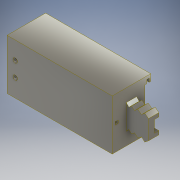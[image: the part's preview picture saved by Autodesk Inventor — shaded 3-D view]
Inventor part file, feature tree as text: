
AUTODESK INVENTOR PART (.ipt)
format: ipt  version: 2018 (Build 220112000, 112)  size: 280,576 bytes
history: native  units: mm
features: extrude x8, sketch x8, projected_geometry x3, mirror x2, other x2, plane x1, reference x1
ambient origin geometry x8: Origin, YZ Plane, XZ Plane, XY Plane, X Axis, Y Axis, Z Axis, Center Point
bodies: 实体1 (feature_tree)
feature tree (25):
  extrude  "拉伸1"  Depth=15.0mm
  extrude  "拉伸2"  Depth=67.0mm
  extrude  "拉伸3"  Depth=26.0mm TaperAngle=0.0deg
  mirror  "镜像1"
  extrude  "拉伸4"  Depth=1.5mm
  plane  "工作平面1"
  mirror  "镜像2"
  extrude  "拉伸5"  Depth=15.0mm
  extrude  "拉伸6"  Depth=65.0mm TaperAngle=0.0deg
  extrude  "拉伸7"  Depth=9.5mm TaperAngle=0.0deg
  extrude  "拉伸8"  Depth=8.0mm
  sketch  "草图1"  dims[d1=6.5mm d2=15.0mm]
  sketch  "草图2"  dims[d3=17.280505mm d4=67.0mm]
  projected_geometry  "投影回路2"
  sketch  "草图3"  dims[d6=17.0mm d7=26.0mm d8=0.0mm]
  sketch  "草图4"  dims[d9=20.0mm d11=1.5mm]
  projected_geometry  "投影回路3"
  sketch  "草图5"  dims[d12=1.5mm d13=15.0mm]
  sketch  "草图6"  dims[d14=2.0mm d15=65.0mm d16=0.0mm]
  projected_geometry  "投影回路4"
  reference  "参考1"
  sketch  "草图7"  dims[d17=4.0mm d18=0.0mm d19=9.5mm d20=0.0mm]
  sketch  "草图8"  dims[d21=9.5mm d22=0.0mm d23=8.0mm d24=3.0mm d25=68.25mm d26=0.0mm d27=3.0mm d28=3.0mm d29=10.0mm d30=1.5mm d31=9.25mm d32=0.0mm d33=2.0mm d34=2.0mm d35=2.0mm d36=5.0mm d37=0.0mm]
  other  "LED组装.iam"
  other  "转动部分:1"
